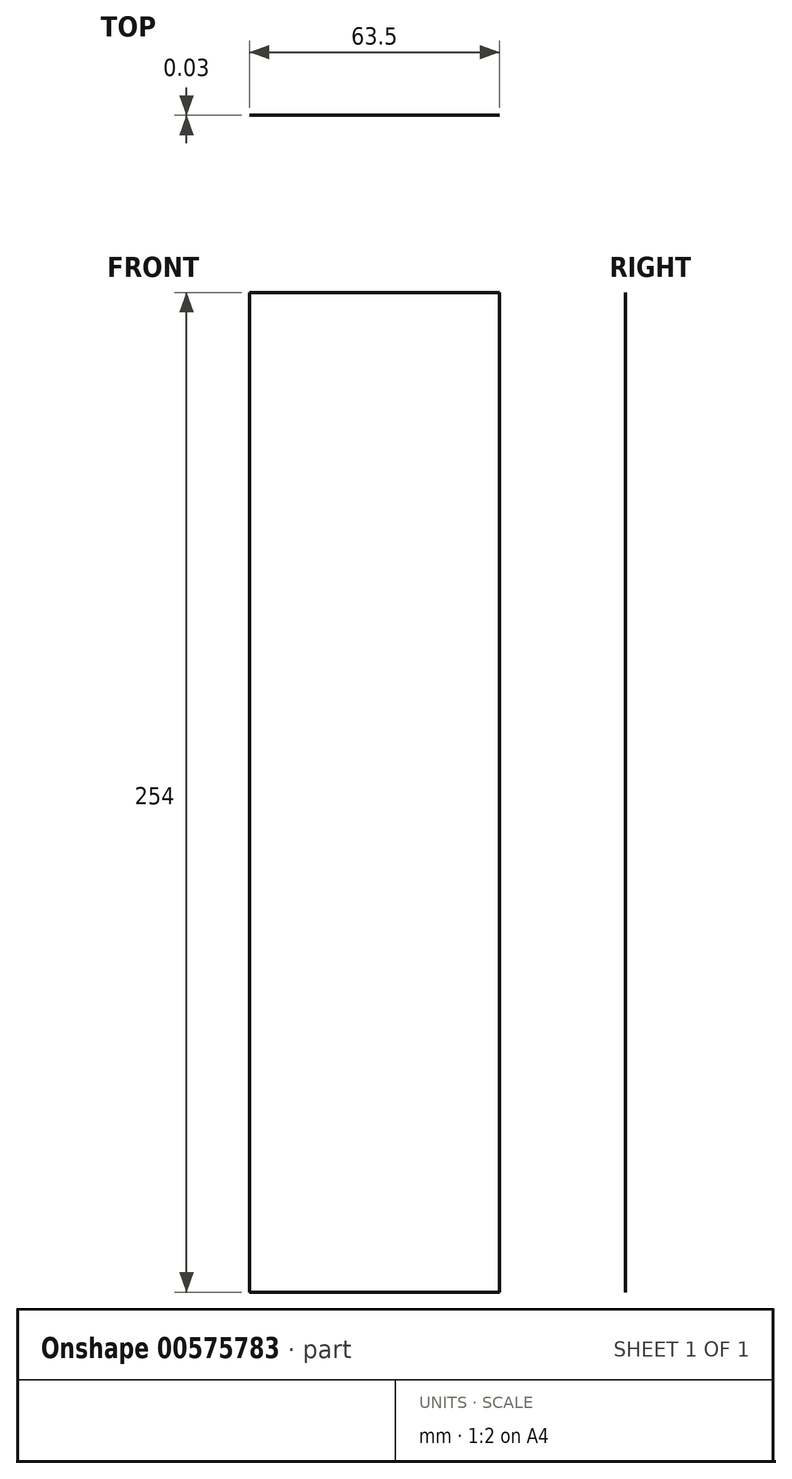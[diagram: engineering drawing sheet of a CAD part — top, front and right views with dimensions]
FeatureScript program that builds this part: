
annotation { "Feature Type Name" : "Feature", "Feature Type Description" : "" }
export const myFeature = defineFeature(function(context is Context, id is Id, definition is map)
    precondition{}
    {
        {
            var Q0;
            Q0=qCreatedBy(makeId("Front.planeOp"),FACE);
            var sketch = newSketch(context, id + "F0", { "sketchPlane" : qUnion([Q0])});
            skLineSegment(sketch, "E0.bottom", {"start": v(-31.75, 127) * mm, "end": v(31.75, 127) * mm});
            skLineSegment(sketch, "E0.top", {"start": v(-31.75, -127) * mm, "end": v(31.75, -127) * mm});
            skLineSegment(sketch, "E0.left", {"start": v(-31.75, 127) * mm, "end": v(-31.75, -127) * mm});
            skLineSegment(sketch, "E0.right", {"start": v(31.75, 127) * mm, "end": v(31.75, -127) * mm});
            skPoint(sketch, "E0.middle", {"position": v(0, 0) * mm});
            skSolve(sketch);
        }
        {
            var Q0;
            Q0 = qSketchRegion(id + "F0", true);
            extrude(context, id + "F1", {"entities" : qUnion([Q0]), "depth" : 3 / 101.6 * mm, "offsetDistance" : 25.4 * mm});
        }
    });
